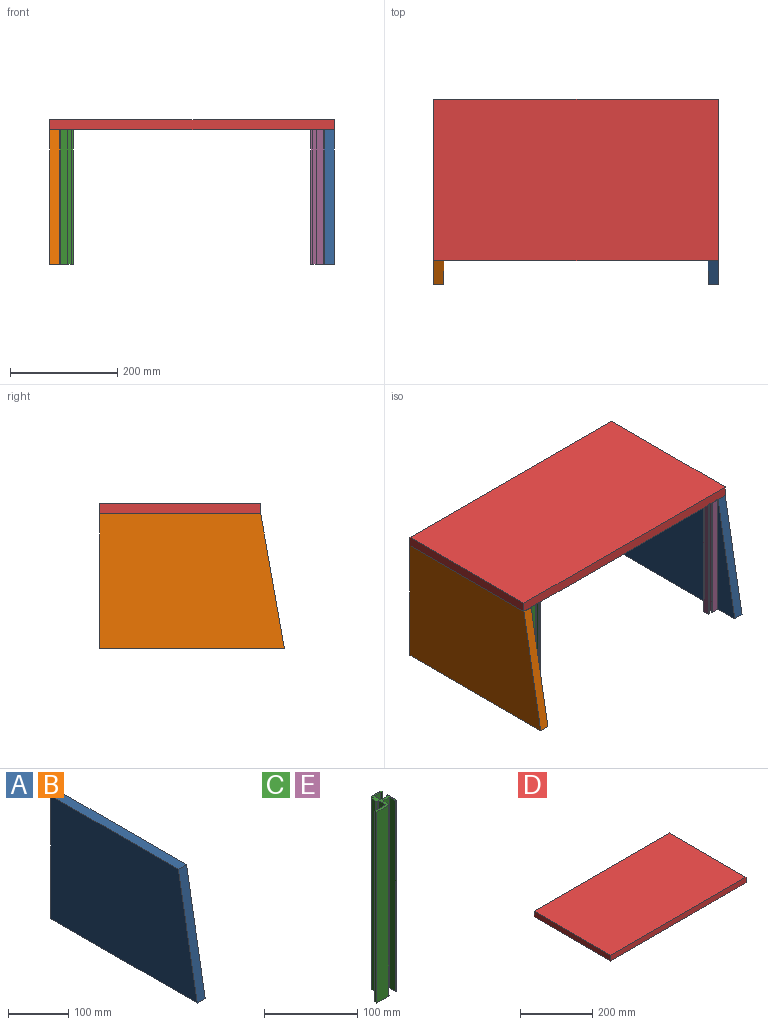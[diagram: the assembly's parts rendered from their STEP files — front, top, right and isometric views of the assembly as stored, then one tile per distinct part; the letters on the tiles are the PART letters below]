
ASSEMBLY  parts=5 mates=12
PART A: 6 faces, bbox 19x344.1x250 mm
  f0: plane 250x44.08mm, normal (0,-0.98,0.17), area 4823.3mm2, adj f1,f3,f4,f5
  f1: plane 344.08x19mm, normal (0,0,-1), area 6537.6mm2, adj f0,f2,f4,f5
  f2: plane 250x19mm, normal (0,1,0), area 4750mm2, adj f1,f3,f4,f5
  f3: plane 300x19mm, normal (0,0,1), area 5700mm2, adj f0,f2,f4,f5
  f4: plane 344.08x250mm, normal (1,0,0), area 80510.2mm2, adj f0,f1,f2,f3
  f5: plane 344.08x250mm, normal (-1,0,0), area 80510.2mm2, adj f0,f1,f2,f3
PART B: same geometry as A
PART C: 32 faces, bbox 31x25x250 mm
  f0: plane 250x0.5mm, normal (0,-1,0), area 125mm2, adj f21,f22,f23,f24
  f1: plane 250x2.5mm, normal (1,0,0), area 625mm2, adj f22,f23,f24,f28
  f2: plane 250x14mm, normal (0,1,0), area 3500mm2, adj f3,f22,f23,f28
  f3: plane 250x3mm, normal (-1,0,0), area 750mm2, adj f2,f4,f22,f23
  f4: plane 250x2mm, normal (0,1,0), area 500mm2, adj f3,f22,f23,f25
  f5: plane 250x6mm, normal (-1,0,0), area 1500mm2, adj f22,f23,f25,f26
  f6: plane 250x2mm, normal (0,-1,0), area 500mm2, adj f7,f22,f23,f26
  f7: plane 250x11mm, normal (-1,0,0), area 2750mm2, adj f6,f8,f22,f23
  f8: plane 250x16.5mm, normal (0,1,0), area 4125mm2, adj f7,f9,f22,f23
  f9: plane 250x3mm, normal (-1,0,0), area 750mm2, adj f8,f10,f22,f23
  f10: plane 250x18mm, normal (0,-1,0), area 4500mm2, adj f9,f22,f23,f31
  f11: plane 250x7.5mm, normal (1,0,0), area 1875mm2, adj f22,f23,f27,f31
  f12: plane 250x9mm, normal (0,-1,0), area 2250mm2, adj f13,f22,f23,f27
  f13: plane 250x9.3mm, normal (-1,0,0), area 2325mm2, adj f12,f22,f23,f29
  f14: plane 250x0.1mm, normal (0,-1,0), area 25mm2, adj f22,f23,f29,f30
  f15: plane 250x14.3mm, normal (1,0,0), area 3575mm2, adj f16,f22,f23,f30
  f16: plane 250x1.5mm, normal (0,1,0), area 375mm2, adj f15,f17,f22,f23
  f17: plane 250x2mm, normal (-1,0,0), area 500mm2, adj f16,f18,f22,f23
  f18: plane 250x10mm, normal (0,1,0), area 2500mm2, adj f17,f19,f22,f23
  f19: plane 250x10mm, normal (1,0,0), area 2500mm2, adj f18,f20,f22,f23
  f20: plane 250x10mm, normal (0,-1,0), area 2500mm2, adj f19,f21,f22,f23
  f21: plane 250x2mm, normal (-1,0,0), area 500mm2, adj f0,f20,f22,f23
  f22: plane 31x25mm, normal (0,0,1), area 225.8mm2, adj f0,f1,f2,f3,f4,f5,f6,f7
  f23: plane 31x25mm, normal (0,0,-1), area 225.8mm2, adj f0,f1,f2,f3,f4,f5,f6,f7
  f24: cylinder r=1mm len=250mm, axis (0,0,-1), area 392.7mm2, adj f0,f1,f22,f23
  f25: cylinder r=1mm len=250mm, axis (0,0,-1), area 392.7mm2, adj f4,f5,f22,f23
  f26: cylinder r=1mm len=250mm, axis (0,0,-1), area 392.7mm2, adj f5,f6,f22,f23
  f27: cylinder r=1mm len=250mm, axis (0,0,1), area 392.7mm2, adj f11,f12,f22,f23
  f28: plane 250x0.5mm, normal (0.71,0.71,0), area 176.8mm2, adj f1,f2,f22,f23
  f29: cylinder r=0.7mm len=250mm, axis (0,0,-1), area 274.9mm2, adj f13,f14,f22,f23
  f30: cylinder r=0.7mm len=250mm, axis (0,0,-1), area 274.9mm2, adj f14,f15,f22,f23
  f31: cylinder r=1.5mm len=250mm, axis (0,0,-1), area 589mm2, adj f10,f11,f22,f23
PART D: 6 faces, bbox 530x300x19 mm
  f0: plane 300x19mm, normal (-1,0,0), area 5700mm2, adj f1,f3,f4,f5
  f1: plane 530x19mm, normal (0,-1,0), area 10070mm2, adj f0,f2,f4,f5
  f2: plane 300x19mm, normal (1,0,0), area 5700mm2, adj f1,f3,f4,f5
  f3: plane 530x19mm, normal (0,1,0), area 10070mm2, adj f0,f2,f4,f5
  f4: plane 530x300mm, normal (0,0,1), area 159000mm2, adj f0,f1,f2,f3
  f5: plane 530x300mm, normal (0,0,-1), area 159000mm2, adj f0,f1,f2,f3
PART E: same geometry as C
PLACE A t=(-530,11.27,-112.65)mm
PLACE B t=(-1041,11.27,-112.65)mm
PLACE C rot(axis=(0,0,-1),90deg) t=(-1022,42.27,-112.65)mm
PLACE D t=(-511,11.27,137.35)mm
PLACE E rot(axis=(-0.71,0.71,0),180deg) t=(-530,42.27,137.35)mm
MATE planar C.f23 <-> B.f1  axis (0,0,-1) through (-1010.65,23.77,-112.65)mm
MATE planar E.f15 <-> D.f1  axis (0,-1,0) through (-537.85,11.27,12.35)mm
MATE planar E.f10 <-> A.f5  axis (1,0,0) through (-530,33.27,12.35)mm
MATE planar C.f15 <-> D.f1  axis (0,-1,0) through (-1014.15,11.27,12.35)mm
MATE planar C.f10 <-> B.f4  axis (-1,0,0) through (-1022,33.27,12.35)mm
MATE planar B.f5 <-> D.f0  axis (-1,0,0) through (-1041,150,9.5)mm
MATE planar B.f3 <-> D.f5  axis (0,0,1) through (-1031.5,161.27,137.35)mm
MATE planar D.f3 <-> B.f2  axis (0,1,0) through (-776,311.27,146.85)mm
MATE planar A.f2 <-> D.f3  axis (0,1,0) through (-520.5,311.27,12.35)mm
MATE planar E.f22 <-> A.f1  axis (0,0,-1) through (-541.35,23.77,-112.65)mm
MATE planar D.f5 <-> A.f3  axis (0,0,-1) through (-776,161.27,137.35)mm
MATE planar A.f4 <-> D.f2  axis (1,0,0) through (-511,150,9.5)mm
